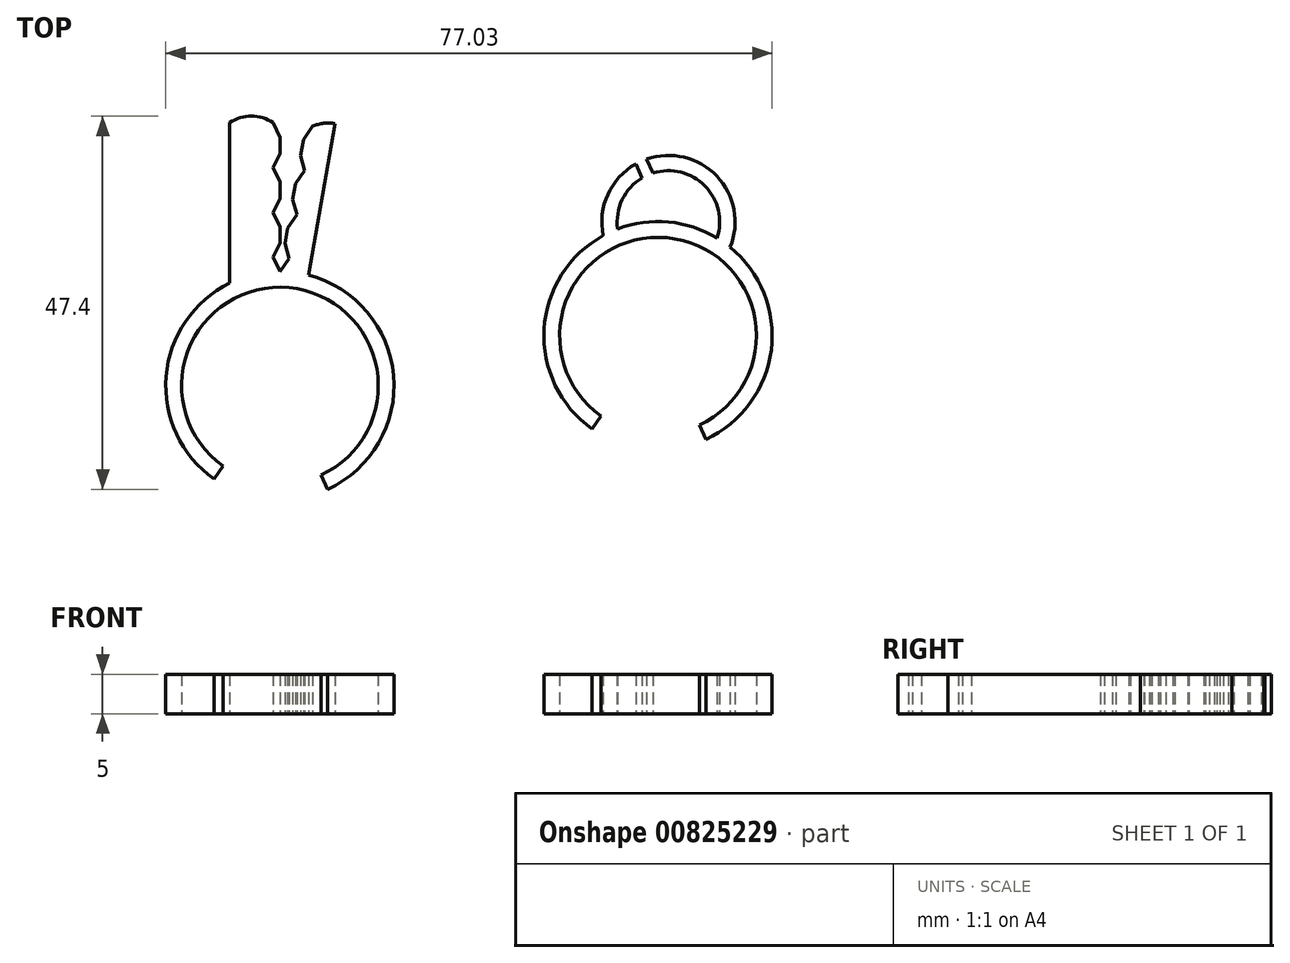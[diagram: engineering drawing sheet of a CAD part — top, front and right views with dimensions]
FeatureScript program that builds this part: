
annotation { "Feature Type Name" : "Feature", "Feature Type Description" : "" }
export const myFeature = defineFeature(function(context is Context, id is Id, definition is map)
    precondition{}
    {
        {
            var Q0;
            Q0=qCreatedBy(makeId("Top.planeOp"),FACE);
            var sketch = newSketch(context, id + "F0", { "sketchPlane" : qUnion([Q0])});
            skArc(sketch, "E0", {"start": v(5.24, -11.35) * mm, "mid": v(1.14, 12.45) * mm, "end": v(-7.21, -10.21) * mm});
            skArc(sketch, "E1", {"start": v(6.07, -13.17) * mm, "mid": v(1.32, 14.44) * mm, "end": v(-8.36, -11.84) * mm});
            skLineSegment(sketch, "E2", {"start": v(-7.21, -10.21) * mm, "end": v(-8.36, -11.84) * mm});
            skLineSegment(sketch, "E3", {"start": v(5.24, -11.35) * mm, "end": v(6.07, -13.17) * mm});
            skPoint(sketch, "E4.orphan", {"position": v(1.61, 13.42) * mm});
            skPoint(sketch, "E5.orphan", {"position": v(1.84, 13.9) * mm});
            skLineSegment(sketch, "E6", {"start": v(0, 14.5) * mm, "end": v(-0.85, 16.32) * mm});
            skLineSegment(sketch, "E7", {"start": v(-0.85, 16.32) * mm, "end": v(0, 18.09) * mm});
            skLineSegment(sketch, "E8", {"start": v(0, 18.09) * mm, "end": v(0, 20.14) * mm});
            skLineSegment(sketch, "E9", {"start": v(0, 20.14) * mm, "end": v(-0.85, 22.01) * mm});
            skLineSegment(sketch, "E10.1.0.0", {"start": v(-0.85, 22.01) * mm, "end": v(0, 23.78) * mm});
            skLineSegment(sketch, "E10.1.0.1", {"start": v(0, 23.78) * mm, "end": v(0, 25.84) * mm});
            skLineSegment(sketch, "E10.1.0.2", {"start": v(0, 25.84) * mm, "end": v(-0.85, 27.7) * mm});
            skLineSegment(sketch, "E10.2.0.0", {"start": v(-0.85, 27.7) * mm, "end": v(0, 29.48) * mm});
            skLineSegment(sketch, "E10.2.0.1", {"start": v(0, 29.48) * mm, "end": v(0, 31.53) * mm});
            skLineSegment(sketch, "E10.2.0.2", {"start": v(0, 31.53) * mm, "end": v(-0.85, 33.4) * mm});
            skLineSegment(sketch, "E10.direction1", {"start": v(-0.85, 16.32) * mm, "end": v(-0.85, 22.01) * mm, "construction": true});
            skArc(sketch, "E11", {"start": v(-0.85, 33.4) * mm, "mid": v(-3.6, 34.23) * mm, "end": v(-6.37, 33.4) * mm});
            skLineSegment(sketch, "E12", {"start": v(-6.37, 33.4) * mm, "end": v(-6.37, 13.03) * mm});
            skLineSegment(sketch, "E13", {"start": v(0, 14.5) * mm, "end": v(1.8, 34.85) * mm});
            skLineSegment(sketch, "E14.MirrorCS", {"start": v(3, 31.26) * mm, "end": v(4.17, 32.95) * mm});
            skLineSegment(sketch, "E15.MirrorCS", {"start": v(2.64, 29.24) * mm, "end": v(3, 31.26) * mm});
            skLineSegment(sketch, "E16.MirrorCS", {"start": v(3.16, 27.35) * mm, "end": v(2.64, 29.24) * mm});
            skLineSegment(sketch, "E17.MirrorCS", {"start": v(2, 25.66) * mm, "end": v(3.16, 27.35) * mm});
            skLineSegment(sketch, "E18.MirrorCS", {"start": v(1.63, 23.64) * mm, "end": v(2, 25.66) * mm});
            skLineSegment(sketch, "E19.MirrorCS", {"start": v(2.16, 21.74) * mm, "end": v(1.63, 23.64) * mm});
            skLineSegment(sketch, "E20.MirrorCS", {"start": v(1, 20.05) * mm, "end": v(2.16, 21.74) * mm});
            skLineSegment(sketch, "E21.MirrorCS", {"start": v(0.63, 18.03) * mm, "end": v(1, 20.05) * mm});
            skLineSegment(sketch, "E22.MirrorCS", {"start": v(1.16, 16.14) * mm, "end": v(0.63, 18.03) * mm});
            skLineSegment(sketch, "E23.MirrorCS", {"start": v(0, 14.5) * mm, "end": v(1.16, 16.14) * mm});
            skArc(sketch, "E24.MirrorCS", {"start": v(4.17, 32.95) * mm, "mid": v(5.57, 33.33) * mm, "end": v(7.03, 33.29) * mm});
            skLineSegment(sketch, "E25", {"start": v(7.03, 33.29) * mm, "end": v(3.64, 14.04) * mm});
            skPoint(sketch, "E26.orphan", {"position": v(9.6, 31.98) * mm});
            skArc(sketch, "E27", {"start": v(53.27, -5) * mm, "mid": v(49.17, 18.8) * mm, "end": v(40.82, -3.86) * mm});
            skArc(sketch, "E28", {"start": v(54.1, -6.82) * mm, "mid": v(62.42, 4.53) * mm, "end": v(57.2, 17.59) * mm});
            skLineSegment(sketch, "E29", {"start": v(40.82, -3.86) * mm, "end": v(39.67, -5.5) * mm});
            skLineSegment(sketch, "E30", {"start": v(53.27, -5) * mm, "end": v(54.1, -6.82) * mm});
            skArc(sketch, "E31", {"start": v(57.2, 17.59) * mm, "mid": v(55.5, 26.6) * mm, "end": v(46.58, 28.79) * mm});
            skArc(sketch, "E32", {"start": v(55.54, 18.75) * mm, "mid": v(54, 25.36) * mm, "end": v(47.4, 27) * mm});
            skLineSegment(sketch, "E33", {"start": v(45.2, 28.16) * mm, "end": v(46.03, 26.4) * mm});
            skLineSegment(sketch, "E34", {"start": v(46.58, 28.79) * mm, "end": v(47.4, 27) * mm});
            skArc(sketch, "E35.trimOffspring", {"start": v(45.2, 28.16) * mm, "mid": v(41.65, 24.3) * mm, "end": v(41.07, 19.06) * mm});
            skArc(sketch, "E36.trimOffspring", {"start": v(46.03, 26.4) * mm, "mid": v(43.49, 23.62) * mm, "end": v(42.9, 19.9) * mm});
            skArc(sketch, "E37.trimOffspring", {"start": v(41.07, 19.06) * mm, "mid": v(33.56, 7.17) * mm, "end": v(39.67, -5.5) * mm});
            skArc(sketch, "E38.trimOffspring", {"start": v(55.54, 18.75) * mm, "mid": v(49.36, 20.79) * mm, "end": v(42.9, 19.9) * mm});
            skSolve(sketch);
        }
        {
            var Q0;
            Q0 = qSketchRegion(id + "F0", true);
            extrude(context, id + "F1", {"entities" : qUnion([Q0]), "depth" : 5 * mm, "offsetDistance" : 25 * mm});
        }
    });
